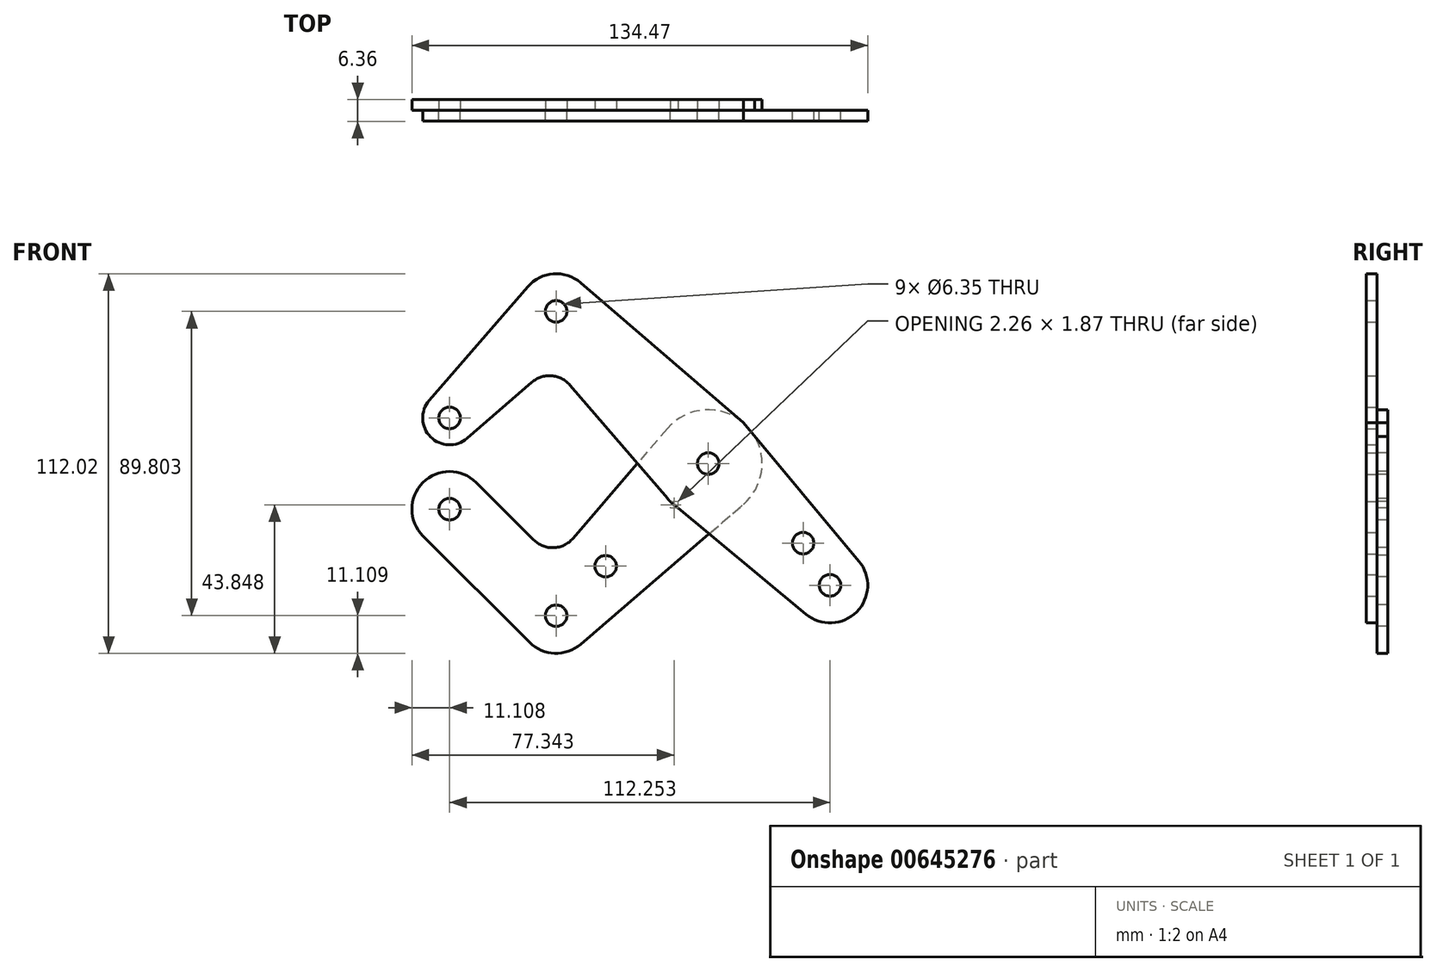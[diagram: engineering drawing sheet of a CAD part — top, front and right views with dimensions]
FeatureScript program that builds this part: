
annotation { "Feature Type Name" : "Feature", "Feature Type Description" : "" }
export const myFeature = defineFeature(function(context is Context, id is Id, definition is map)
    precondition{}
    {
        {
            var Q0;
            Q0=qCreatedBy(makeId("Front.planeOp"),FACE);
            var sketch = newSketch(context, id + "F0", { "sketchPlane" : qUnion([Q0])});
            skCircle(sketch, "E0", {"center": v(-76.33, 13.47) * mm, "radius": 7.94 * mm});
            skCircle(sketch, "E1", {"center": v(-44.9, 44.9) * mm, "radius": 11.11 * mm});
            skCircle(sketch, "E2", {"center": v(-76.33, 13.47) * mm, "radius": 3.18 * mm});
            skCircle(sketch, "E3", {"center": v(-44.9, 44.9) * mm, "radius": 3.18 * mm});
            skCircle(sketch, "E4", {"center": v(0, 0) * mm, "radius": 15.88 * mm});
            skLineSegment(sketch, "E5", {"start": v(-44.9, 44.9) * mm, "end": v(85.66, -85.66) * mm, "construction": true});
            skLineSegment(sketch, "E6", {"start": v(-44.9, 44.9) * mm, "end": v(-76.33, 13.47) * mm, "construction": true});
            skCircle(sketch, "E7", {"center": v(35.92, -35.92) * mm, "radius": 11.11 * mm});
            skCircle(sketch, "E8", {"center": v(35.92, -35.92) * mm, "radius": 3.18 * mm});
            skCircle(sketch, "E9", {"center": v(27.97, -23.48) * mm, "radius": 3.18 * mm});
            skLineSegment(sketch, "E10", {"start": v(0, 0) * mm, "end": v(-44.9, -44.9) * mm, "construction": true});
            skCircle(sketch, "E11", {"center": v(-30.3, -30.3) * mm, "radius": 3.18 * mm});
            skCircle(sketch, "E12", {"center": v(-44.9, -44.9) * mm, "radius": 11.11 * mm});
            skLineSegment(sketch, "E13", {"start": v(-44.9, -44.9) * mm, "end": v(-76.33, -13.47) * mm, "construction": true});
            skCircle(sketch, "E14", {"center": v(-76.33, -13.47) * mm, "radius": 11.11 * mm});
            skCircle(sketch, "E15", {"center": v(-76.33, -13.47) * mm, "radius": 3.18 * mm});
            skCircle(sketch, "E16", {"center": v(-44.9, -44.9) * mm, "radius": 3.18 * mm});
            skLineSegment(sketch, "E17", {"start": v(-82.33, 18.67) * mm, "end": v(-53.3, 52.18) * mm});
            skLineSegment(sketch, "E18", {"start": v(-37.66, 53.33) * mm, "end": v(10.35, 12.04) * mm});
            skLineSegment(sketch, "E19", {"start": v(10.35, 12.04) * mm, "end": v(44.45, -28.8) * mm});
            skLineSegment(sketch, "E20", {"start": v(28.82, -44.47) * mm, "end": v(-11.23, -11.23) * mm});
            skLineSegment(sketch, "E21", {"start": v(-71.13, 7.47) * mm, "end": v(-52.08, 23.98) * mm});
            skLineSegment(sketch, "E22", {"start": v(-40.85, 23.15) * mm, "end": v(-12.04, -10.35) * mm});
            skArc(sketch, "E23.filletArc", {"start": v(-40.85, 23.15) * mm, "mid": v(-46.3, 25.9) * mm, "end": v(-52.08, 23.98) * mm});
            skLineSegment(sketch, "E24", {"start": v(-84.19, -21.33) * mm, "end": v(-52.76, -52.76) * mm});
            skLineSegment(sketch, "E25", {"start": v(-37.66, -53.33) * mm, "end": v(10.35, -12.04) * mm});
            skLineSegment(sketch, "E26", {"start": v(-12.04, 10.35) * mm, "end": v(-39.93, -22.07) * mm});
            skLineSegment(sketch, "E27", {"start": v(-68.47, -5.61) * mm, "end": v(-51.57, -22.51) * mm});
            skArc(sketch, "E28.filletArc", {"start": v(-51.57, -22.51) * mm, "mid": v(-45.65, -24.84) * mm, "end": v(-39.93, -22.07) * mm});
            skCircle(sketch, "E29", {"center": v(0, 0) * mm, "radius": 3.18 * mm});
            skSolve(sketch);
        }
        {
            var Q0;
            {var subQ0=sQuery(id+"F0.wireOp",EDGE,"E17");Q0=makeQuery(id+"F0.imprint","IMPRINT",FACE,{"disambiguationData":[TD([[makeQuery(id+"F0.imprint","IMPRINT",EDGE,{"derivedFrom":subQ0}),-1.0]])]});}
            var Q1;
            Q1=makeQuery(id+"F0.imprint","IMPRINT",FACE,{"disambiguationData":[TD([[makeQuery(id+"F0.imprint","IMPRINT",EDGE,{"derivedFrom":sQuery(id+"F0.wireOp",EDGE,"E3")}),-1.0]])]});
            var Q2;
            Q2=makeQuery(id+"F0.imprint","IMPRINT",FACE,{"disambiguationData":[TD([[makeQuery(id+"F0.imprint","IMPRINT",EDGE,{"derivedFrom":sQuery(id+"F0.wireOp",EDGE,"E2")}),-1.0]])]});
            var Q3;
            {var subQ0=sQuery(id+"F0.wireOp",EDGE,"E4");var subQ5=makeQuery(id+"F0.imprint","INTERSECT",VERTEX,{"derivedFrom":[subQ0,sQuery(id+"F0.wireOp",EDGE,"E22")]});Q3=makeQuery(id+"F0.imprint","IMPRINT",FACE,{"disambiguationData":[TD([[makeQuery(id+"F0.imprint","IMPRINT",EDGE,{"disambiguationData":[TD([[subQ5,1.0]])],"derivedFrom":subQ0}),1.0]])]});}
            var Q4;
            Q4=makeQuery(id+"F0.imprint","IMPRINT",FACE,{"disambiguationData":[TD([[makeQuery(id+"F0.imprint","IMPRINT",EDGE,{"derivedFrom":sQuery(id+"F0.wireOp",EDGE,"E9")}),-1.0]])]});
            var Q5;
            Q5=makeQuery(id+"F0.imprint","IMPRINT",FACE,{"disambiguationData":[TD([[makeQuery(id+"F0.imprint","IMPRINT",EDGE,{"derivedFrom":sQuery(id+"F0.wireOp",EDGE,"E8")}),-1.0]])]});
            var Q6;
            {var subQ0=sQuery(id+"F0.wireOp",EDGE,"E25");var subQ1=sQuery(id+"F0.wireOp",EDGE,"E4");var subQ2=makeQuery(id+"F0.imprint","INTERSECT",VERTEX,{"derivedFrom":[subQ1,subQ0]});Q6=makeQuery(id+"F0.imprint","IMPRINT",FACE,{"disambiguationData":[TD([[makeQuery(id+"F0.imprint","IMPRINT",EDGE,{"disambiguationData":[TD([[subQ2,1.0]])],"derivedFrom":subQ1}),-1.0]])]});}
            var Q7;
            {var subQ0=sQuery(id+"F0.wireOp",EDGE,"E22");var subQ1=sQuery(id+"F0.wireOp",EDGE,"E4");var subQ2=makeQuery(id+"F0.imprint","INTERSECT",VERTEX,{"derivedFrom":[subQ1,subQ0]});Q7=makeQuery(id+"F0.imprint","IMPRINT",FACE,{"disambiguationData":[TD([[makeQuery(id+"F0.imprint","IMPRINT",EDGE,{"disambiguationData":[TD([[subQ2,1.0]])],"derivedFrom":subQ1}),-1.0]])]});}
            extrude(context, id + "F1", {"entities" : qUnion([Q0, Q1, Q2, Q3, Q4, Q5, Q6, Q7]), "depth" : 3.17 * mm, "offsetDistance" : 25.4 * mm});
        }
        {
            var Q0;
            Q0=makeQuery(id+"F0.imprint","IMPRINT",FACE,{"disambiguationData":[TD([[makeQuery(id+"F0.imprint","IMPRINT",EDGE,{"derivedFrom":sQuery(id+"F0.wireOp",EDGE,"E15")}),-1.0]])]});
            var Q1;
            Q1=makeQuery(id+"F0.imprint","IMPRINT",FACE,{"disambiguationData":[TD([[makeQuery(id+"F0.imprint","IMPRINT",EDGE,{"derivedFrom":sQuery(id+"F0.wireOp",EDGE,"E11")}),-1.0]])]});
            var Q2;
            Q2=makeQuery(id+"F0.imprint","IMPRINT",FACE,{"disambiguationData":[TD([[makeQuery(id+"F0.imprint","IMPRINT",EDGE,{"derivedFrom":sQuery(id+"F0.wireOp",EDGE,"E16")}),-1.0]])]});
            var Q3;
            Q3=makeQuery(id+"F0.imprint","IMPRINT",FACE,{"disambiguationData":[TD([[makeQuery(id+"F0.imprint","IMPRINT",EDGE,{"derivedFrom":sQuery(id+"F0.wireOp",EDGE,"E29")}),-1.0]])]});
            var Q4;
            {var subQ0=sQuery(id+"F0.wireOp",EDGE,"E22");var subQ1=sQuery(id+"F0.wireOp",EDGE,"E4");var subQ2=makeQuery(id+"F0.imprint","INTERSECT",VERTEX,{"derivedFrom":[subQ1,subQ0]});Q4=makeQuery(id+"F0.imprint","IMPRINT",FACE,{"disambiguationData":[TD([[makeQuery(id+"F0.imprint","IMPRINT",EDGE,{"disambiguationData":[TD([[subQ2,1.0]])],"derivedFrom":subQ1}),-1.0]])]});}
            var Q5;
            {var subQ0=sQuery(id+"F0.wireOp",EDGE,"E25");var subQ1=sQuery(id+"F0.wireOp",EDGE,"E4");var subQ2=makeQuery(id+"F0.imprint","INTERSECT",VERTEX,{"derivedFrom":[subQ1,subQ0]});Q5=makeQuery(id+"F0.imprint","IMPRINT",FACE,{"disambiguationData":[TD([[makeQuery(id+"F0.imprint","IMPRINT",EDGE,{"disambiguationData":[TD([[subQ2,1.0]])],"derivedFrom":subQ1}),-1.0]])]});}
            extrude(context, id + "F2", {"entities" : qUnion([Q0, Q1, Q2, Q3, Q4, Q5]), "oppositeDirection" : true, "depth" : 3.17 * mm, "offsetDistance" : 25.4 * mm});
        }
    });
